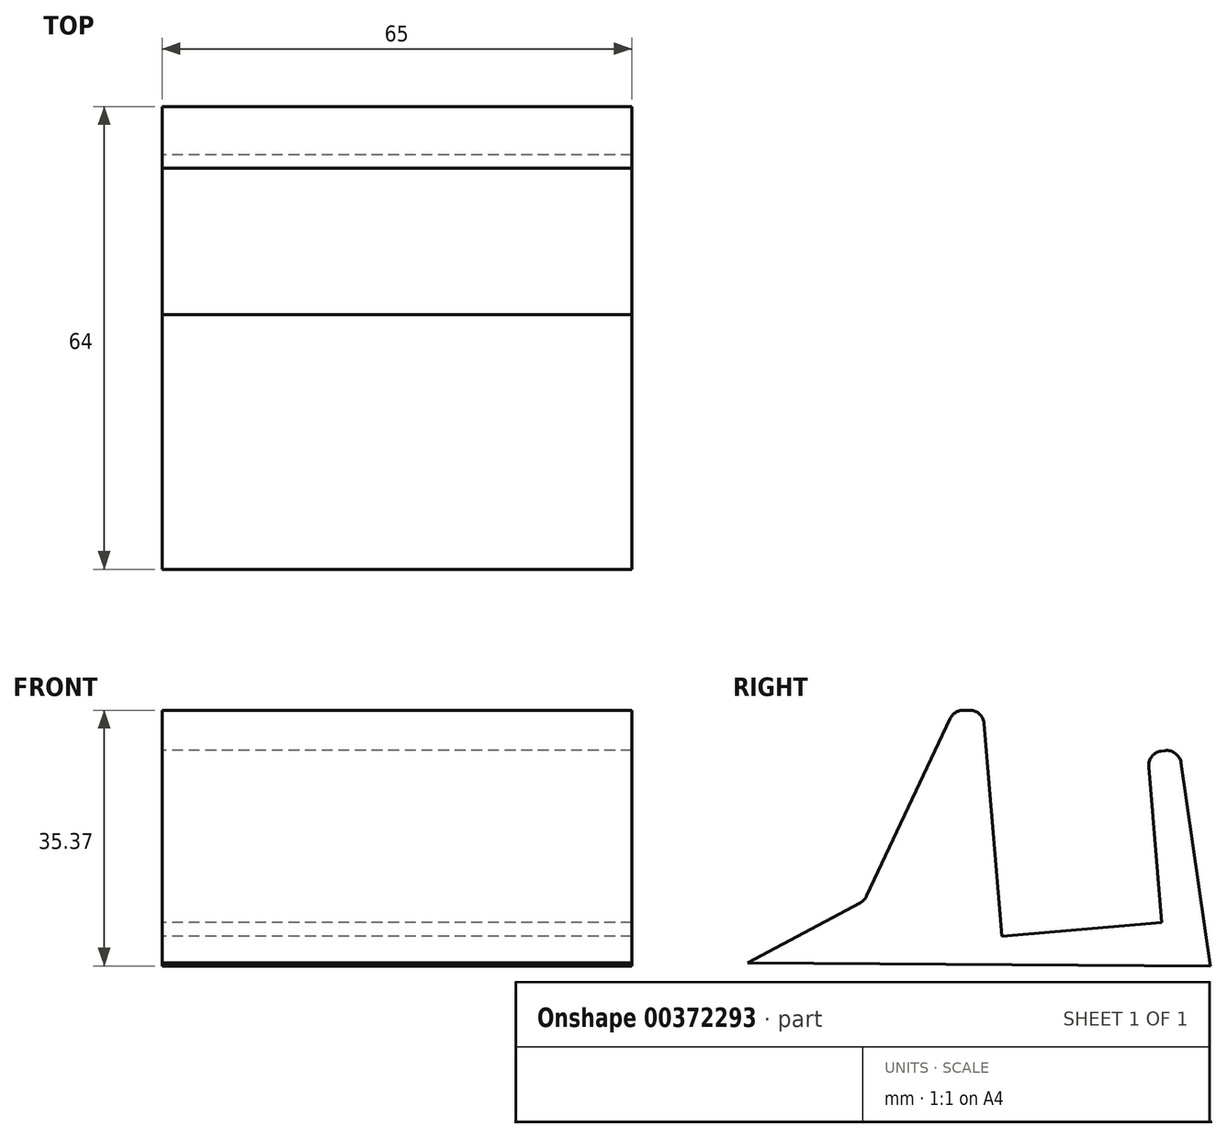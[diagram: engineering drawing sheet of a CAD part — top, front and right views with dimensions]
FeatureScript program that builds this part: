
annotation { "Feature Type Name" : "Feature", "Feature Type Description" : "" }
export const myFeature = defineFeature(function(context is Context, id is Id, definition is map)
    precondition{}
    {
        {
            var Q0;
            Q0=qCreatedBy(makeId("Right.planeOp"),FACE);
            var sketch = newSketch(context, id + "F0", { "sketchPlane" : qUnion([Q0])});
            skPoint(sketch, "E0.0", {"position": v(135.92, 33.43) * mm});
            skPoint(sketch, "E1.0", {"position": v(140.27, 34.06) * mm});
            skPoint(sketch, "E2.0", {"position": v(137.9, 10) * mm});
            skPoint(sketch, "E3.0", {"position": v(115.8, 8.13) * mm});
            skPoint(sketch, "E4.0", {"position": v(96.76, 13.07) * mm});
            skLineSegment(sketch, "E5", {"start": v(137.9, 10) * mm, "end": v(135.92, 33.43) * mm});
            skPoint(sketch, "E6.0", {"position": v(144.6, 4) * mm});
            skLineSegment(sketch, "E7", {"start": v(140.27, 34.06) * mm, "end": v(144.6, 4) * mm});
            skLineSegment(sketch, "E8", {"start": v(135.92, 33.43) * mm, "end": v(140.27, 34.06) * mm});
            skLineSegment(sketch, "E9", {"start": v(115.8, 8.13) * mm, "end": v(137.9, 10) * mm});
            skLineSegment(sketch, "E10", {"start": v(144.6, 4) * mm, "end": v(80.6, 4.4) * mm});
            skLineSegment(sketch, "E11", {"start": v(80.6, 4.4) * mm, "end": v(96.76, 13.07) * mm});
            skLineSegment(sketch, "E12", {"start": v(115.8, 8.13) * mm, "end": v(113.16, 39.37) * mm});
            skLineSegment(sketch, "E13", {"start": v(113.16, 39.37) * mm, "end": v(109.16, 39.37) * mm});
            skLineSegment(sketch, "E14", {"start": v(109.16, 39.37) * mm, "end": v(96.76, 13.07) * mm});
            skSolve(sketch);
        }
        {
            var Q0;
            Q0 = qSketchRegion(id + "F0", true);
            extrude(context, id + "F1", {"entities" : qUnion([Q0]), "depth" : 65 * mm, "offsetDistance" : 25 * mm});
        }
        {
            var Q0;
            Q0=makeQuery(id+"F1.opExtrude","SWEPT_EDGE",EDGE,{"disambiguationData":[OSD([sQuery(id+"F0.wireOp",EDGE,"E13"),sQuery(id+"F0.wireOp",EDGE,"E14")])]});
            var Q1;
            Q1=makeQuery(id+"F1.opExtrude","SWEPT_EDGE",EDGE,{"disambiguationData":[OSD([sQuery(id+"F0.wireOp",EDGE,"E12"),sQuery(id+"F0.wireOp",EDGE,"E13")])]});
            var Q2;
            Q2=makeQuery(id+"F1.opExtrude","SWEPT_EDGE",EDGE,{"disambiguationData":[OSD([sQuery(id+"F0.wireOp",EDGE,"E5"),sQuery(id+"F0.wireOp",EDGE,"E8")])]});
            var Q3;
            Q3=makeQuery(id+"F1.opExtrude","SWEPT_EDGE",EDGE,{"disambiguationData":[OSD([sQuery(id+"F0.wireOp",EDGE,"E7"),sQuery(id+"F0.wireOp",EDGE,"E8")])]});
            var Q4;
            Q4=makeQuery(id+"F1.opExtrude","SWEPT_EDGE",EDGE,{"disambiguationData":[OSD([sQuery(id+"F0.wireOp",EDGE,"E11"),sQuery(id+"F0.wireOp",EDGE,"E14")])]});
            fillet(context, id + "F2", {"entities" : qUnion([Q0, Q1, Q2, Q3, Q4]), "radius" : 2 * mm, "tangentPropagation" : true, "allowEdgeOverflow" : false});
        }
    });
